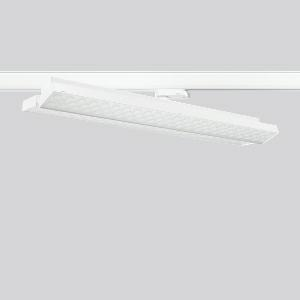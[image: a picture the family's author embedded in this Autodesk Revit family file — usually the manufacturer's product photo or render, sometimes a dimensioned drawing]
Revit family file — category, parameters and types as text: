
# Revit family: tx-move_742162_002_76_3dfe
name_source: partatom
category: Lighting Fixtures
units: mm (PartAtom-declared; Revit-internal decimal feet)

## family parameters
Cut with Voids When Loaded = No
Host = Face
Light Source = No
Part Type = Normal
Room Calculation Point = No
Round Connector Dimension = Use Diameter
Shared = No

## types (1)
- MultiLumen 1 (1 x LED Modul 830, 2925 lm, 3000)
    Apparent Load = 41 VA
    CIE Flux Codes = 77 96 99 100 100
    Color Rendering = 80
    Color Temperature = 3000
    Default Elevation = 1800 mm
    Description = Series: TX-MOVE
Multifunctional surface-mounted spotlight for area lighting. Very flat design. Housing: sheet steel, powder-coated. Rotation range: 356°. Swivel range: 90°. Consistent alignment possible with visible tilt scale. High-efficiency LED units with optimum light control thanks to clear plastic (PC) lens optics. Spezielle Mikrostrukturen reduzieren Gelbsaum. Symmetrical light distribution. With adapter for RZB 3-circuit DALI tracks. Suitable for Track on ceiling. MultiLumen: Luminous flux adjustable in 3 steps. Factory setting is the highest luminous flux. Environmentally friendly and resource-saving due to replaceable and recyclable components. 
Colour: traffic white, matt (RAL 9016)
Length: 570 mm
Width: 119 mm
Height: 88 mm
Lamp: LED
Socket: without socket
Colour temperature: 3000K
Colour rendering index (CRI): 80
System power: 41 W
Rated luminous flux: 5850 lm
Luminous efficiency: 143 lm/W
System power 2: 57 W
Rated luminous flux 2: 7950 lm
Luminous efficiency 2: 139 lm/W
System power 3: 73 W
Rated luminous flux 3: 9700 lm
Luminous efficiency 3: 133 lm/W
Control gear: Dimmable EVG, DALI
Protection class: I
Type of protection: IP 20
    Height = 75 mm
    Lamp = 1 x LED Modul 830
    Lamp Light Flux = 2925 lm
    Lamp count = 1
    Length = 569 mm
    Lifetime = 50000 h
    Luminous efficacy = 143 lm/W
    Manufacturer = RZB
    ModVariant = No
    Model = 742162.002.76
    Mounting Place = Ceiling
    Mounting Type = Surface mounted
    Number of Poles = 1
    OnlyDefault = Yes
    Power Factor = 1
    Product Name = TX-MOVE
    Product group = Track mounted projectors
    ProductGroupID = 301
    Protection Class = Protection class I
    Protection Degree = IP 20
    RLX_Detail_Level = 1
    RLX_Emergency_Light_Flux = 0 lm
    RLX_Emergency_Type = 0
    RLX_Emergency_Type_DB = No
    RlxData = <blob elided: 31013 chars, md5=9cc5e9b7>
    Socket = socket
    Standby Power = 0 W
    System Light Flux = 5850 lm
    System Power = 41 W
    Type Comments = MultiLumen 1
    Type Image = 742162.002.jpg
    URL = http://relux.com
    VarID = multilumen_1
    Voltage = 0 V
    Weight = 0.00 kg
    Width = 119 mm

## geometry (parser evidence)
native form markers: Blend x4, Sweep x15
no freeform markers — native parametric forms only
